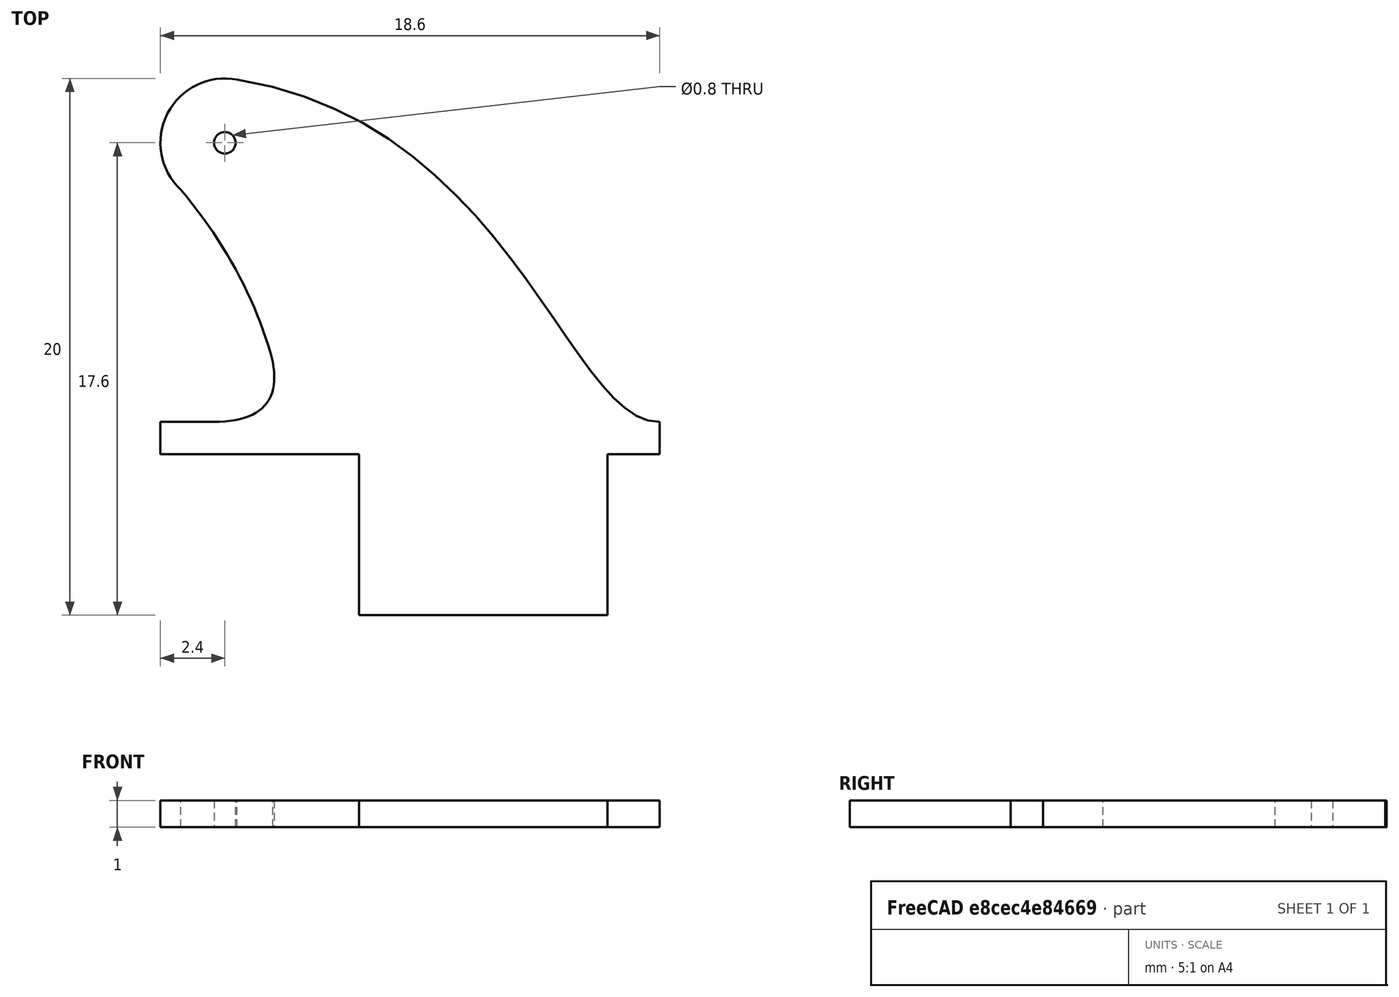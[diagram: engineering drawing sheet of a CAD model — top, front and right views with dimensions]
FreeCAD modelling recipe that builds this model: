
FCSTD DOCUMENT  (FreeCAD 0.20R0.20.2)
Label: 004
License: All rights reserved
LicenseURL: http://en.wikipedia.org/wiki/All_rights_reserved
objects: Sketcher::SketchObject×2, Part::Extrusion×1
note: 3 computed .brp shape members not serialized (recipe doc carries the construction recipe); baked Part::Feature solids carry a one-line shape summary decoded from their .brp

FEATURE [Sketcher::SketchObject] Sketch  label="main"
  FullyConstrained = true
  sketch-geometry (25):
    g0: LineSegment StartX=12.0586 StartY=-6 StartZ=0 EndX=12.0586 EndY=0 EndZ=0
    g1: LineSegment StartX=2.8 StartY=-6 StartZ=0 EndX=2.8 EndY=0 EndZ=0
    g2: LineSegment StartX=2.8 StartY=-6 StartZ=0 EndX=12.0586 EndY=-6 EndZ=0
    g3: LineSegment StartX=12.0586 StartY=0 StartZ=0 EndX=14 EndY=0 EndZ=0
    g4: LineSegment StartX=2.8 StartY=0 StartZ=0 EndX=0 EndY=0 EndZ=0
    g5: LineSegment StartX=14 StartY=0 StartZ=0 EndX=14 EndY=1.2 EndZ=0
    g6: LineSegment StartX=0 StartY=0 StartZ=0 EndX=-4.6 EndY=0 EndZ=0
    g7: Circle CenterX=-2.2 CenterY=11.6 CenterZ=0 NormalX=0 NormalY=0 NormalZ=1 AngleXU=0 Radius=0.4
    g8-g11: Circle x4 (B-spline internal-alignment scaffolding for g12; pole/knot coordinates omitted)
    g12: BSplineCurve PolesCount=4 KnotsCount=2 Degree=3 IsPeriodic=0
    g13: GeomPoint X=-1.74436 Y=13.9564 Z=0
    g14: GeomPoint X=14 Y=1.2 Z=0
    g15: ArcOfCircle CenterX=-2.2 CenterY=11.6 CenterZ=0 NormalX=0 NormalY=0 NormalZ=1 AngleXU=0 Radius=2.4 StartAngle=1.37979 EndAngle=3.95565
    g16: LineSegment StartX=-2.62672 StartY=1.2 StartZ=0 EndX=-4.6 EndY=1.2 EndZ=0
    g17: LineSegment StartX=-4.6 StartY=0 StartZ=0 EndX=-4.6 EndY=1.2 EndZ=0
    g18: Circle CenterX=-2.62672 CenterY=1.2 CenterZ=0 NormalX=0 NormalY=0 NormalZ=1 AngleXU=0 Radius=1
    g19: Circle CenterX=0 CenterY=1.2 CenterZ=0 NormalX=0 NormalY=0 NormalZ=1 AngleXU=0 Radius=1
    g20: Circle CenterX=-0.413885 CenterY=3.44541 CenterZ=0 NormalX=0 NormalY=0 NormalZ=1 AngleXU=0 Radius=1
    g21: BSplineCurve PolesCount=3 KnotsCount=2 Degree=2 IsPeriodic=0
    g22: GeomPoint X=-2.62672 Y=1.2 Z=0
    g23: GeomPoint X=-0.413885 Y=3.44541 Z=0
    g24: BSplineCurve PolesCount=3 KnotsCount=2 Degree=2 IsPeriodic=0
  constraints (52):
    c: Vertical(g0)
    c: Vertical(g1)
    c: Block(g1)
    c: Block(g0)
    c: Distance(g1) = 6
    c: Coincident(g2,g1)
    c: Horizontal(g2)
    c: Coincident(g0,g2)
    c: Block(g2)
    c: Coincident(g3,g0)
    c: Horizontal(g3)
    c: Coincident(g4,g1)
    c: Horizontal(g4)
    c: Block(g3)
    c: Block(g4)
    c: Coincident(g5,g3)
    c: Vertical(g5)
    c: Distance(g5) = 1.2
    c: Coincident(g6,g4)
    c: Horizontal(g6)
    c: Distance(g6) = 4.6
    c: Block(g7)
    c: Weight(g8) = 1
    c: Equal(g8,g9)
    c: Equal(g8,g10)
    c: Equal(g8,g11)
    c: Coincident(g12,g5)
    c: InternalAlignment(g8-g11 -> g12) x4
    c: InternalAlignment(g13,g12)
    c: InternalAlignment(g14,g12)
    c: Block(g12)
    c: Coincident(g15,g7)
    c: Coincident(g15,g12)
    c: Coincident(g15,g24)
    c: Block(g15)
    c: Horizontal(g16)
    c: Coincident(g17,g6)
    c: Vertical(g17)
    c: Coincident(g17,g16)
    c: Weight(g18) = 1
    c: Equal(g18,g19)
    c: Equal(g18,g20)
    c: InternalAlignment(g18,g21)
    c: InternalAlignment(g19,g21)
    c: InternalAlignment(g20,g21)
    c: InternalAlignment(g22,g21)
    c: InternalAlignment(g23,g21)
    c: Block(g16)
    c: Coincident(g16,g21)
    c: Coincident(g21,g24)
    c: Block(g24)
    c: Block(g21)
FEATURE [Part::Extrusion] Extrude
  Base = -> Sketch
  Dir = (0,0,1)
  DirMode = 2
  FaceMakerClass = Part::FaceMakerBullseye
  LengthFwd = 1
  LengthRev = 0
  Solid = true
  Symmetric = false
FEATURE [Sketcher::SketchObject] Sketch001  label="main001"
  FullyConstrained = true
  sketch-geometry (25):
    g0: LineSegment StartX=12.0586 StartY=-6 StartZ=0 EndX=12.0586 EndY=0 EndZ=0
    g1: LineSegment StartX=2.8 StartY=-6 StartZ=0 EndX=2.8 EndY=0 EndZ=0
    g2: LineSegment StartX=2.8 StartY=-6 StartZ=0 EndX=12.0586 EndY=-6 EndZ=0
    g3: LineSegment StartX=12.0586 StartY=0 StartZ=0 EndX=14 EndY=0 EndZ=0
    g4: LineSegment StartX=2.8 StartY=0 StartZ=0 EndX=0 EndY=0 EndZ=0
    g5: LineSegment StartX=14 StartY=0 StartZ=0 EndX=14 EndY=1.2 EndZ=0
    g6: LineSegment StartX=0 StartY=0 StartZ=0 EndX=-4.6 EndY=0 EndZ=0
    g7: Circle CenterX=-2.2 CenterY=11.6 CenterZ=0 NormalX=0 NormalY=0 NormalZ=1 AngleXU=0 Radius=0.4
    g8-g11: Circle x4 (B-spline internal-alignment scaffolding for g12; pole/knot coordinates omitted)
    g12: BSplineCurve PolesCount=4 KnotsCount=2 Degree=3 IsPeriodic=0
    g13: GeomPoint X=-1.74436 Y=13.9564 Z=0
    g14: GeomPoint X=14 Y=1.2 Z=0
    g15: ArcOfCircle CenterX=-2.2 CenterY=11.6 CenterZ=0 NormalX=0 NormalY=0 NormalZ=1 AngleXU=0 Radius=2.4 StartAngle=1.37979 EndAngle=3.95565
    g16: LineSegment StartX=-2.62672 StartY=1.2 StartZ=0 EndX=-4.6 EndY=1.2 EndZ=0
    g17: LineSegment StartX=-4.6 StartY=0 StartZ=0 EndX=-4.6 EndY=1.2 EndZ=0
    g18: Circle CenterX=-2.62672 CenterY=1.2 CenterZ=0 NormalX=0 NormalY=0 NormalZ=1 AngleXU=0 Radius=1
    g19: Circle CenterX=0 CenterY=1.2 CenterZ=0 NormalX=0 NormalY=0 NormalZ=1 AngleXU=0 Radius=1
    g20: Circle CenterX=-0.413885 CenterY=3.44541 CenterZ=0 NormalX=0 NormalY=0 NormalZ=1 AngleXU=0 Radius=1
    g21: BSplineCurve PolesCount=3 KnotsCount=2 Degree=2 IsPeriodic=0
    g22: GeomPoint X=-2.62672 Y=1.2 Z=0
    g23: GeomPoint X=-0.413885 Y=3.44541 Z=0
    g24: BSplineCurve PolesCount=3 KnotsCount=2 Degree=2 IsPeriodic=0
  constraints (52):
    c: Vertical(g0)
    c: Vertical(g1)
    c: Block(g1)
    c: Block(g0)
    c: Distance(g1) = 6
    c: Coincident(g2,g1)
    c: Horizontal(g2)
    c: Coincident(g0,g2)
    c: Block(g2)
    c: Coincident(g3,g0)
    c: Horizontal(g3)
    c: Coincident(g4,g1)
    c: Horizontal(g4)
    c: Block(g3)
    c: Block(g4)
    c: Coincident(g5,g3)
    c: Vertical(g5)
    c: Distance(g5) = 1.2
    c: Coincident(g6,g4)
    c: Horizontal(g6)
    c: Distance(g6) = 4.6
    c: Block(g7)
    c: Weight(g8) = 1
    c: Equal(g8,g9)
    c: Equal(g8,g10)
    c: Equal(g8,g11)
    c: Coincident(g12,g5)
    c: InternalAlignment(g8-g11 -> g12) x4
    c: InternalAlignment(g13,g12)
    c: InternalAlignment(g14,g12)
    c: Block(g12)
    c: Coincident(g15,g7)
    c: Coincident(g15,g12)
    c: Coincident(g15,g24)
    c: Block(g15)
    c: Horizontal(g16)
    c: Coincident(g17,g6)
    c: Vertical(g17)
    c: Coincident(g17,g16)
    c: Weight(g18) = 1
    c: Equal(g18,g19)
    c: Equal(g18,g20)
    c: InternalAlignment(g18,g21)
    c: InternalAlignment(g19,g21)
    c: InternalAlignment(g20,g21)
    c: InternalAlignment(g22,g21)
    c: InternalAlignment(g23,g21)
    c: Block(g16)
    c: Coincident(g16,g21)
    c: Coincident(g21,g24)
    c: Block(g24)
    c: Block(g21)
